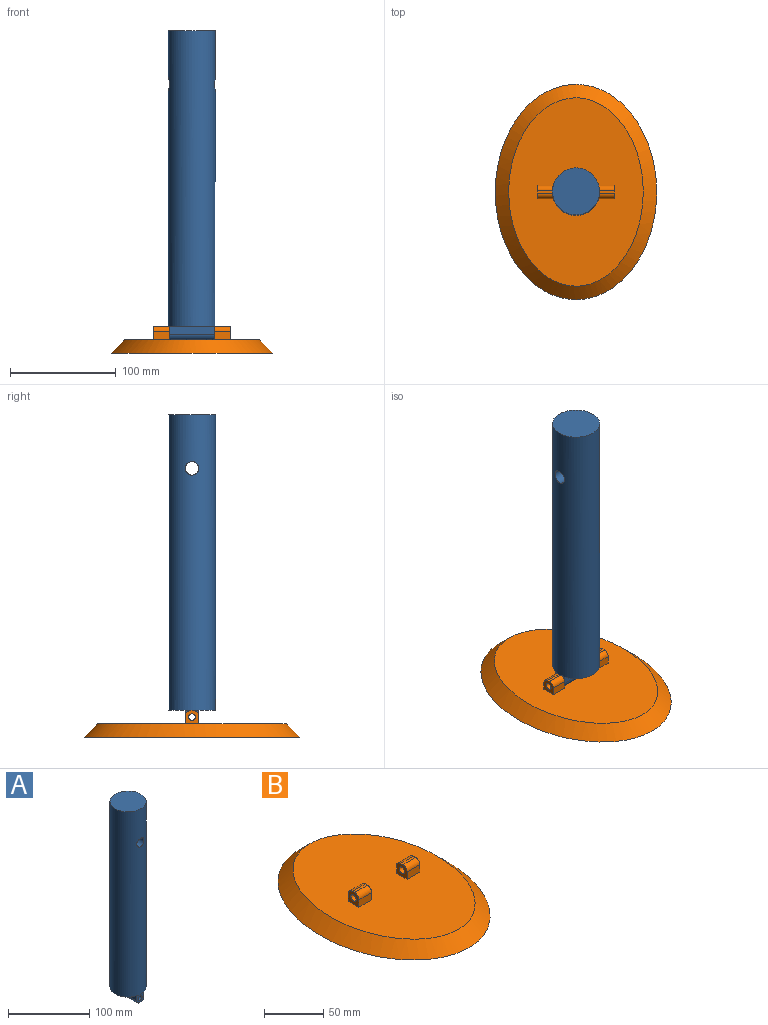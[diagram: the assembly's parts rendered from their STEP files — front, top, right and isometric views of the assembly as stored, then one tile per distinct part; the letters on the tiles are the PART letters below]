
ASSEMBLY  parts=2 mates=1
PART A: 15 faces, bbox 44.5x44.5x292.1 mm
  f0: plane 42.6x15.88mm, normal (0,0,-1), area 497.5mm2, adj f3,f7
  f1: plane 42.6x15.88mm, normal (0,0,-1), area 497.5mm2, adj f3,f9
  f2: plane 12.7x0.93mm, normal (0,0,-1), area 7.9mm2, adj f3,f8
  f3: cylinder r=22.23mm len=279.4mm, axis (0,0,-1), area 38760.4mm2, adj f0,f1,f2,f4,f5,f6
  f4: plane 44.45x44.45mm, normal (0,0,1), area 1551.8mm2, adj f3
  f5: plane 12.7x0.93mm, normal (0,0,-1), area 7.9mm2, adj f3,f10
  f6: cylinder r=6.35mm len=44.45mm, axis (0,-1,0), area 1736.7mm2, adj f3
  f7: plane 42.6x7.62mm, normal (1,0,0), area 324.6mm2, adj f0,f8,f10,f13
  f8: plane 12.7x12.7mm, normal (0,-1,0), area 118.5mm2, adj f2,f7,f9,f11,f12,f13,f14
  f9: plane 42.6x7.62mm, normal (-1,0,0), area 324.6mm2, adj f1,f8,f10,f12
  f10: plane 12.7x12.7mm, normal (0,1,0), area 118.5mm2, adj f5,f7,f9,f11,f12,f13,f14
  f11: plane 42.6x2.54mm, normal (0,0,-1), area 108.2mm2, adj f8,f10,f12,f13
  f12: cylinder r=5.08mm len=42.6mm, axis (0,-1,0), area 339.9mm2, adj f8,f9,f10,f11
  f13: cylinder r=5.08mm len=42.6mm, axis (0,1,0), area 339.9mm2, adj f7,f8,f10,f11
  f14: cylinder r=3.17mm len=42.6mm, axis (0,-1,0), area 849.8mm2, adj f8,f10
PART B: 19 faces, bbox 152.7x203.5x25.7 mm
  f0: plane 178.09x127.29mm, normal (0,0,1), area 17318.3mm2, adj f2,f3,f4,f5,f6,f8,f9,f10
  f1: plane 203.2x152.4mm, normal (0,0,-1), area 24320.2mm2, adj f2
  f2: bspline ~203.2x152.4mm, area 9366.4mm2, adj f0,f1
  f3: plane 15.24x7.62mm, normal (0,-1,0), area 116.1mm2, adj f0,f4,f6,f16
  f4: plane 12.7x12.7mm, normal (1,0,0), area 118.5mm2, adj f0,f3,f5,f7,f15,f16,f18
  f5: plane 15.24x7.62mm, normal (0,1,0), area 116.1mm2, adj f0,f4,f6,f15
  f6: plane 12.7x12.7mm, normal (-1,0,0), area 118.5mm2, adj f0,f3,f5,f7,f15,f16,f18
  f7: plane 15.24x2.54mm, normal (0,0,1), area 38.7mm2, adj f4,f6,f15,f16
  f8: plane 15.24x7.62mm, normal (0,1,0), area 116.1mm2, adj f0,f9,f11,f14
  f9: plane 12.7x12.7mm, normal (-1,0,0), area 118.5mm2, adj f0,f8,f10,f12,f13,f14,f17
  f10: plane 15.24x7.62mm, normal (0,-1,0), area 116.1mm2, adj f0,f9,f11,f13
  f11: plane 12.7x12.7mm, normal (1,0,0), area 118.5mm2, adj f0,f8,f10,f12,f13,f14,f17
  f12: plane 15.24x2.54mm, normal (0,0,1), area 38.7mm2, adj f9,f11,f13,f14
  f13: cylinder r=5.08mm len=15.24mm, axis (-1,0,0), area 121.6mm2, adj f9,f10,f11,f12
  f14: cylinder r=5.08mm len=15.24mm, axis (1,0,0), area 121.6mm2, adj f8,f9,f11,f12
  f15: cylinder r=5.08mm len=15.24mm, axis (1,0,0), area 121.6mm2, adj f4,f5,f6,f7
  f16: cylinder r=5.08mm len=15.24mm, axis (-1,0,0), area 121.6mm2, adj f3,f4,f6,f7
  f17: cylinder r=3.17mm len=15.24mm, axis (-1,0,0), area 304mm2, adj f9,f11
  f18: cylinder r=3.17mm len=15.24mm, axis (-1,0,0), area 304mm2, adj f4,f6
PLACE A rot(axis=(0,0,-1),90deg) t=(-0.59,-0.05,13.17)mm
PLACE B t=(-0.59,-0.05,-12.23)mm fixed
MATE revolute A.f14 <-> B.f17  axis (-1,0,0) through (-21.89,-0.05,6.82)mm
